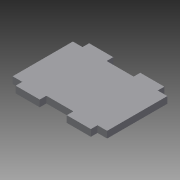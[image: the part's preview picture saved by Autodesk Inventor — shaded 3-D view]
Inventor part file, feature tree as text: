
AUTODESK INVENTOR PART (.ipt)
format: ipt  version: 2015 (Build 190159000, 159)  size: 91,136 bytes
history: native  units: mm
features: extrude x1, sketch x1
ambient origin geometry x8: Origin, YZ Plane, XZ Plane, XY Plane, X Axis, Y Axis, Z Axis, Center Point
bodies: Solid1 (feature_tree)
feature tree (2):
  extrude  "Extrusion1"  Depth=20.0mm
  sketch  "Sketch1"  dims[d2=5.5mm d3=20.0mm d4=5.5mm d5=20.0mm d6=90.0deg d16=5.5mm d17=0.0mm d18=8.0mm d20=8.0mm]
